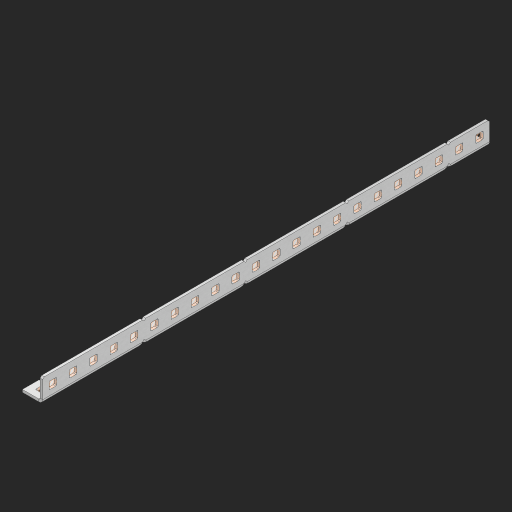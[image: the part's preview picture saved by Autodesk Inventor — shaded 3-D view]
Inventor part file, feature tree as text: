
AUTODESK INVENTOR PART (.ipt)
format: ipt  version: 2023 (Build 270158000, 158)  size: 1,041,408 bytes
history: native  units: in
note: dims shown in document units (in); Inventor stores cm internally (conversion verified against a paired STEP export)
features: other x214, extrude x64, sheet_metal_op x11, sketch x10, pattern_linear x2, mirror x1, chamfer x1
ambient origin geometry x8: Origin, YZ Plane, XZ Plane, XY Plane, X Axis, Y Axis, Z Axis, Center Point
bodies: Solid1 (feature_tree), Body (feature_tree)
feature tree (303):
  other  "Alu Half C 1x2x1x22"
  other  "Table"
  other  "Alu C 1x2x1x35"
  other  "Alu C 1x2x1x34"
  other  "Alu C 1x2x1x33"
  other  "Alu C 1x2x1x32"
  other  "Alu C 1x2x1x31"
  other  "Alu C 1x2x1x30"
  other  "Alu C 1x2x1x29"
  other  "Alu C 1x2x1x28"
  other  "Alu C 1x2x1x27"
  other  "Alu C 1x2x1x26"
  other  "Alu C 1x2x1x25"
  other  "Alu C 1x2x1x24"
  other  "Alu C 1x2x1x23"
  other  "Alu C 1x2x1x22"
  other  "Alu C 1x2x1x21"
  other  "Alu C 1x2x1x20"
  other  "Alu C 1x2x1x19"
  other  "Alu C 1x2x1x18"
  other  "Alu C 1x2x1x17"
  other  "Alu C 1x2x1x16"
  other  "Alu C 1x2x1x15"
  other  "Alu C 1x2x1x14"
  other  "Alu C 1x2x1x13"
  other  "Alu C 1x2x1x12"
  other  "Alu C 1x2x1x11"
  other  "Alu C 1x2x1x10"
  other  "Alu C 1x2x1x9"
  other  "Alu C 1x2x1x8"
  other  "Alu C 1x2x1x7"
  other  "Alu C 1x2x1x6"
  other  "Alu C 1x2x1x5"
  other  "Alu C 1x2x1x4"
  other  "Alu C 1x2x1x3"
  other  "Alu C 1x2x1x2"
  other  "Alu C 1x2x1x1"
  other  "Steel C 1x2x1x35"
  other  "Steel C 1x2x1x34"
  other  "Steel C 1x2x1x33"
  other  "Steel C 1x2x1x32"
  other  "Steel C 1x2x1x31"
  other  "Steel C 1x2x1x30"
  other  "Steel C 1x2x1x29"
  other  "Steel C 1x2x1x28"
  other  "Steel C 1x2x1x27"
  other  "Steel C 1x2x1x26"
  other  "Steel C 1x2x1x25"
  other  "Steel C 1x2x1x24"
  other  "Steel C 1x2x1x23"
  other  "Steel C 1x2x1x22"
  other  "Steel C 1x2x1x21"
  other  "Steel C 1x2x1x20"
  other  "Steel C 1x2x1x19"
  other  "Steel C 1x2x1x18"
  other  "Steel C 1x2x1x17"
  other  "Steel C 1x2x1x16"
  other  "Steel C 1x2x1x15"
  other  "Steel C 1x2x1x14"
  other  "Steel C 1x2x1x13"
  other  "Steel C 1x2x1x12"
  other  "Steel C 1x2x1x11"
  other  "Steel C 1x2x1x10"
  other  "Steel C 1x2x1x9"
  other  "Steel C 1x2x1x8"
  other  "Steel C 1x2x1x7"
  other  "Steel C 1x2x1x6"
  other  "Steel C 1x2x1x5"
  other  "Steel C 1x2x1x4"
  other  "Steel C 1x2x1x3"
  other  "Steel C 1x2x1x2"
  other  "Steel C 1x2x1x1"
  other  "Alu Half C 1x2x1x35"
  other  "Alu Half C 1x2x1x34"
  other  "Alu Half C 1x2x1x33"
  other  "Alu Half C 1x2x1x32"
  other  "Alu Half C 1x2x1x31"
  other  "Alu Half C 1x2x1x30"
  other  "Alu Half C 1x2x1x29"
  other  "Alu Half C 1x2x1x28"
  other  "Alu Half C 1x2x1x27"
  other  "Alu Half C 1x2x1x26"
  other  "Alu Half C 1x2x1x25"
  other  "Alu Half C 1x2x1x24"
  other  "Alu Half C 1x2x1x23"
  other  "Alu Half C 1x2x1x21"
  other  "Alu Half C 1x2x1x20"
  other  "Alu Half C 1x2x1x19"
  other  "Alu Half C 1x2x1x18"
  other  "Alu Half C 1x2x1x17"
  other  "Alu Half C 1x2x1x16"
  other  "Alu Half C 1x2x1x15"
  other  "Alu Half C 1x2x1x14"
  other  "Alu Half C 1x2x1x13"
  other  "Alu Half C 1x2x1x12"
  other  "Alu Half C 1x2x1x11"
  other  "Alu Half C 1x2x1x10"
  other  "Alu Half C 1x2x1x9"
  other  "Alu Half C 1x2x1x8"
  other  "Alu Half C 1x2x1x7"
  other  "Alu Half C 1x2x1x6"
  other  "Alu Half C 1x2x1x5"
  other  "Alu Half C 1x2x1x4"
  other  "Alu Half C 1x2x1x3"
  other  "Alu Half C 1x2x1x2"
  other  "Alu Half C 1x2x1x1"
  other  "Steel Half C 1x2x1x35"
  other  "Steel Half C 1x2x1x34"
  other  "Steel Half C 1x2x1x33"
  other  "Steel Half C 1x2x1x32"
  other  "Steel Half C 1x2x1x31"
  other  "Steel Half C 1x2x1x30"
  other  "Steel Half C 1x2x1x29"
  other  "Steel Half C 1x2x1x28"
  other  "Steel Half C 1x2x1x27"
  other  "Steel Half C 1x2x1x26"
  other  "Steel Half C 1x2x1x25"
  other  "Steel Half C 1x2x1x24"
  other  "Steel Half C 1x2x1x23"
  other  "Steel Half C 1x2x1x22"
  other  "Steel Half C 1x2x1x21"
  other  "Steel Half C 1x2x1x20"
  other  "Steel Half C 1x2x1x19"
  other  "Steel Half C 1x2x1x18"
  other  "Steel Half C 1x2x1x17"
  other  "Steel Half C 1x2x1x16"
  other  "Steel Half C 1x2x1x15"
  other  "Steel Half C 1x2x1x14"
  other  "Steel Half C 1x2x1x13"
  other  "Steel Half C 1x2x1x12"
  other  "Steel Half C 1x2x1x11"
  other  "Steel Half C 1x2x1x10"
  other  "Steel Half C 1x2x1x9"
  other  "Steel Half C 1x2x1x8"
  other  "Steel Half C 1x2x1x7"
  other  "Steel Half C 1x2x1x6"
  other  "Steel Half C 1x2x1x5"
  other  "Steel Half C 1x2x1x4"
  other  "Steel Half C 1x2x1x3"
  other  "Steel Half C 1x2x1x2"
  other  "Steel Half C 1x2x1x1"
  sheet_metal_op  "Flanges"
  other  "Flange Pattern Plane"
  other  "Flange Pattern Sketch"
  sheet_metal_op  "Flange Pattern"
  sheet_metal_op  "Body Pattern"
  pattern_linear  "Center Pattern"  Spacing1=0.0625in  [1 undecoded]
  other  "Arc Length"
  mirror  "Notch Mirror"
  pattern_linear  "Notch Pattern"  Spacing1=0.182in  [1 undecoded]
  chamfer  "End Chamfer"
  extrude  "Half Cut"  Depth=0.02in
  sketch  "Sketch1"  dims[d0=1.0in]
  other  "Plate1"
  sketch  "Sketch2"  dims[d1=11.0in]
  other  "Plate2"
  sheet_metal_op  "Bend1"
  sheet_metal_op  "Corner1"
  sketch  "Sketch3"  dims[d2=0.0625in]
  sketch  "Sketch7"  dims[d3=0.0625in]
  other  "Srf1"
  other  "Srf2"
  sketch  "Sketch8"  dims[d4=0.0312in]
  sketch  "Sketch9"  dims[d5=0.125in]
  other  "Srf91"
  sheet_metal_op  "Body Pattern Sketch"
  other  "Srf92"
  sketch  "Sketch13"  dims[d6=0.0625in]
  sketch  "Sketch14"  dims[d7=0.5in d8=90.0deg d9=0.0312in]
  sketch  "Sketch15"  dims[d10=0.25in]
  sketch  "Sketch16"  dims[d11=0.0625in d12=0.0625in d16=0.182in d17=0.02in d18=0.0625in d19=0.0in d20=0.25in d21=0.25in d38=8.6614in d40=0.5in d41=0.3937in d43=1.0in d46=0.172in d47=1.0in d48=0.0in d49=0.182in d50=0.02in d51=0.25in d52=0.25in d53=0.0625in d54=0.0in d55=0.172in d56=1.0in d57=0.0in d58=0.25in d60=8.6614in d62=0.5in d63=0.3937in d65=0.5in d85=0.1473in d86=0.1782in d88=0.04in d89=0.0625in d90=0.0in d91=0.04in d92=0.0491in d95=2.5in d96=0.04in d97=0.25in d98=45.0deg d99=0.25in d100=0.5in d101=0.0in d102=2.497in d106=0.182in d107=0.02in d108=0.5in d109=0.5in d110=0.0625in d111=0.0in d112=0.172in d113=0.5in d114=0.0in d117=0.5in d118=0.5in d119=0.5in]
  other  "Srf786"
  other  "Srf823"
  other  "Srf824"
  other  "Srf825"
  other  "Srf826"
  other  "Srf827"
  other  "Srf828"
  other  "Srf829"
  other  "Srf856"
  other  "Srf857"
  other  "Srf858"
  other  "Srf859"
  other  "Srf860"
  other  "Srf861"
  other  "Srf862"
  other  "Srf889"
  other  "Srf890"
  other  "Srf891"
  other  "Srf892"
  other  "Srf893"
  other  "Srf894"
  other  "Srf895"
  other  "Srf896"
  other  "Srf922"
  other  "Srf923"
  other  "Srf924"
  other  "Srf925"
  other  "Srf926"
  other  "Srf959"
  other  "Srf960"
  other  "Srf961"
  other  "Srf962"
  other  "Srf963"
  other  "Srf996"
  other  "Srf997"
  other  "Srf998"
  other  "Srf999"
  other  "Srf1000"
  other  "Srf1143"
  other  "Srf1144"
  other  "Srf1145"
  other  "Srf1146"
  other  "Srf1147"
  other  "Srf1148"
  other  "Srf1149"
  other  "Srf1150"
  other  "Srf1199"
  other  "Srf1200"
  other  "Srf1201"
  other  "Srf1202"
  other  "Srf1203"
  other  "Srf1204"
  other  "Srf1205"
  other  "Srf1206"
  other  "Srf1255"
  other  "Srf1256"
  other  "Srf1257"
  other  "Srf1258"
  other  "Srf1259"
  other  "Srf1260"
  other  "Srf1261"
  other  "Srf1262"
  sheet_metal_op  "Flange Stamp"
  sheet_metal_op  "Flange Circle"
  sheet_metal_op  "Body Stamp"
  sheet_metal_op  "Body Circle"
  other  "Center Stamp"
  other  "Center Circle"
  sheet_metal_op  "Notch"
  extrude  "ExtrusionSrf2"  Depth=0.0625in
  extrude  "ExtrusionSrf92"  TaperAngle=0.0deg  [1 undecoded]
  extrude  "ExtrusionSrf823"  Depth=0.25in
  extrude  "ExtrusionSrf824"  Depth=0.25in
  extrude  "ExtrusionSrf825"  Depth=0.5in
  extrude  "ExtrusionSrf826"  Depth=0.5in
  extrude  "ExtrusionSrf827"  Depth=1.0in TaperAngle=0.0deg
  extrude  "ExtrusionSrf828"  Depth=0.182in
  extrude  "ExtrusionSrf829"  Depth=0.02in
  extrude  "ExtrusionSrf856"  Depth=0.25in
  extrude  "ExtrusionSrf857"  Depth=0.25in
  extrude  "ExtrusionSrf858"  Depth=0.0625in
  extrude  "ExtrusionSrf859"  TaperAngle=0.0deg  [1 undecoded]
  extrude  "ExtrusionSrf860"  Depth=0.5in
  extrude  "ExtrusionSrf861"  Depth=1.0in TaperAngle=0.0deg
  extrude  "ExtrusionSrf862"  Depth=0.25in
  extrude  "ExtrusionSrf889"  Depth=0.5in
  extrude  "ExtrusionSrf890"  Depth=0.5in
  extrude  "ExtrusionSrf891"  Depth=0.5in
  extrude  "ExtrusionSrf892"  Depth=0.5in
  extrude  "ExtrusionSrf893"  Depth=0.5in
  extrude  "ExtrusionSrf894"  Depth=0.0625in
  extrude  "ExtrusionSrf895"  TaperAngle=0.0deg  [1 undecoded]
  extrude  "ExtrusionSrf896"  Depth=0.5in
  extrude  "ExtrusionSrf922"  Depth=0.5in
  extrude  "ExtrusionSrf923"  Depth=2.5in
  extrude  "ExtrusionSrf924"  Depth=0.25in TaperAngle=45.0deg
  extrude  "ExtrusionSrf925"  Depth=0.25in
  extrude  "ExtrusionSrf926"  Depth=0.5in TaperAngle=0.0deg
  extrude  "ExtrusionSrf959"  Depth=0.5in
  extrude  "ExtrusionSrf960"  Depth=0.182in
  extrude  "ExtrusionSrf961"  Depth=0.02in
  extrude  "ExtrusionSrf962"  Depth=0.5in
  extrude  "ExtrusionSrf963"  Depth=0.5in
  extrude  "ExtrusionSrf996"  Depth=0.0625in
  extrude  "ExtrusionSrf997"  TaperAngle=0.0deg  [1 undecoded]
  extrude  "ExtrusionSrf998"  Depth=0.5in
  extrude  "ExtrusionSrf999"  Depth=0.5in TaperAngle=0.0deg
  extrude  "ExtrusionSrf1000"  Depth=0.5in
  extrude  "ExtrusionSrf1143"  Depth=0.5in
  extrude  "ExtrusionSrf1144"  Depth=0.5in
  extrude  "ExtrusionSrf1145"  [1 undecoded]
  extrude  "ExtrusionSrf1146"  [1 undecoded]
  extrude  "ExtrusionSrf1147"  [1 undecoded]
  extrude  "ExtrusionSrf1148"  [1 undecoded]
  extrude  "ExtrusionSrf1149"  [1 undecoded]
  extrude  "ExtrusionSrf1150"  [1 undecoded]
  extrude  "ExtrusionSrf1199"  [1 undecoded]
  extrude  "ExtrusionSrf1200"  [1 undecoded]
  extrude  "ExtrusionSrf1201"  [1 undecoded]
  extrude  "ExtrusionSrf1202"  [1 undecoded]
  extrude  "ExtrusionSrf1203"  [1 undecoded]
  extrude  "ExtrusionSrf1204"  [1 undecoded]
  extrude  "ExtrusionSrf1205"  [1 undecoded]
  extrude  "ExtrusionSrf1206"  [1 undecoded]
  extrude  "ExtrusionSrf1255"  [1 undecoded]
  extrude  "ExtrusionSrf1256"  [1 undecoded]
  extrude  "ExtrusionSrf1257"  [1 undecoded]
  extrude  "ExtrusionSrf1258"  [1 undecoded]
  extrude  "ExtrusionSrf1259"  [1 undecoded]
  extrude  "ExtrusionSrf1260"  [1 undecoded]
  extrude  "ExtrusionSrf1261"  [1 undecoded]
  extrude  "ExtrusionSrf1262"  [1 undecoded]
note: 28 required parameter values undecoded (feature->parameter linkage not recoverable at this tier; creation-order binding heuristic only, values carry confidence <= 0.55)
